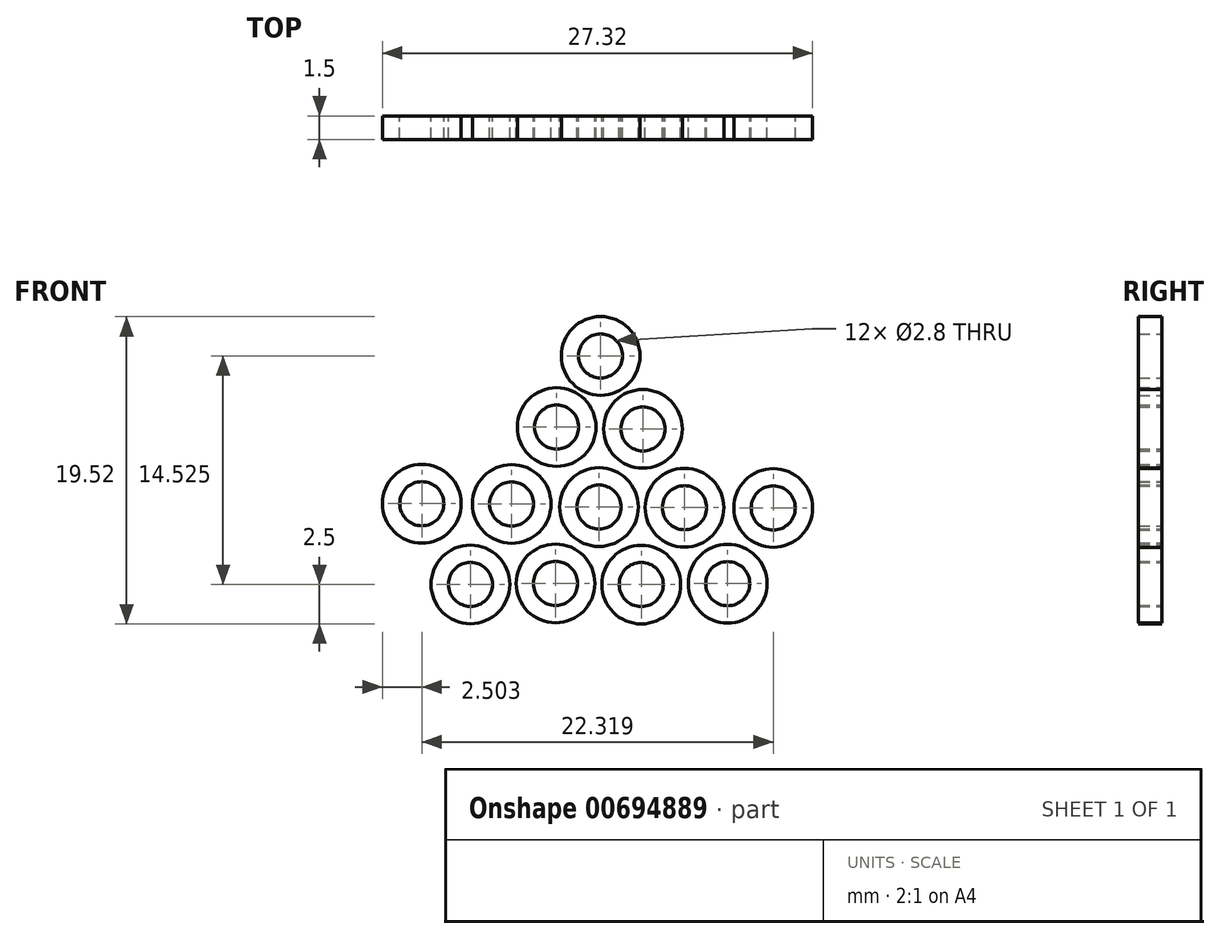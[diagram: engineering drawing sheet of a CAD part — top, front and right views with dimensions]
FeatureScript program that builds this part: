
annotation { "Feature Type Name" : "Feature", "Feature Type Description" : "" }
export const myFeature = defineFeature(function(context is Context, id is Id, definition is map)
    precondition{}
    {
        {
            var Q0;
            Q0=qCreatedBy(makeId("Front.planeOp"),FACE);
            var sketch = newSketch(context, id + "F0", { "sketchPlane" : qUnion([Q0])});
            skCircle(sketch, "E0", {"center": v(0, 0) * mm, "radius": 2.5 * mm});
            skCircle(sketch, "E1", {"center": v(0, 0) * mm, "radius": 1.4 * mm});
            skCircle(sketch, "E2", {"center": v(-2.68, 4.92) * mm, "radius": 2.5 * mm});
            skCircle(sketch, "E3", {"center": v(-2.68, 4.92) * mm, "radius": 1.4 * mm});
            skCircle(sketch, "E4", {"center": v(-5.44, 0.07) * mm, "radius": 2.5 * mm});
            skCircle(sketch, "E5", {"center": v(-5.44, 0.07) * mm, "radius": 1.4 * mm});
            skCircle(sketch, "E6", {"center": v(-13.94, 5.14) * mm, "radius": 2.5 * mm});
            skCircle(sketch, "E7", {"center": v(-13.94, 5.14) * mm, "radius": 1.4 * mm});
            skCircle(sketch, "E8", {"center": v(5.5, 0.06) * mm, "radius": 2.5 * mm});
            skCircle(sketch, "E9", {"center": v(5.5, 0.06) * mm, "radius": 1.4 * mm});
            skCircle(sketch, "E10", {"center": v(8.38, 4.87) * mm, "radius": 2.5 * mm});
            skCircle(sketch, "E11", {"center": v(8.38, 4.87) * mm, "radius": 1.4 * mm});
            skCircle(sketch, "E12", {"center": v(-5.37, 10) * mm, "radius": 2.5 * mm});
            skCircle(sketch, "E13", {"center": v(-5.37, 10) * mm, "radius": 1.4 * mm});
            skCircle(sketch, "E14", {"center": v(0.1, 9.9) * mm, "radius": 2.5 * mm});
            skCircle(sketch, "E15", {"center": v(0.1, 9.9) * mm, "radius": 1.4 * mm});
            skCircle(sketch, "E16", {"center": v(2.75, 4.88) * mm, "radius": 2.5 * mm});
            skCircle(sketch, "E17", {"center": v(2.75, 4.88) * mm, "radius": 1.4 * mm});
            skCircle(sketch, "E18", {"center": v(-8.23, 5.12) * mm, "radius": 2.5 * mm});
            skCircle(sketch, "E19", {"center": v(-8.23, 5.12) * mm, "radius": 1.4 * mm});
            skCircle(sketch, "E20", {"center": v(-10.85, 0.01) * mm, "radius": 2.5 * mm});
            skCircle(sketch, "E21", {"center": v(-10.85, 0.01) * mm, "radius": 1.4 * mm});
            skCircle(sketch, "E22", {"center": v(-2.58, 14.52) * mm, "radius": 2.5 * mm});
            skCircle(sketch, "E23", {"center": v(-2.58, 14.52) * mm, "radius": 1.4 * mm});
            skSolve(sketch);
        }
        {
            var Q0;
            Q0=makeQuery(id+"F0.imprint","IMPRINT",FACE,{"disambiguationData":[TD([[makeQuery(id+"F0.imprint","IMPRINT",EDGE,{"derivedFrom":sQuery(id+"F0.wireOp",EDGE,"E6")}),1.0]])]});
            var Q1;
            Q1=makeQuery(id+"F0.imprint","IMPRINT",FACE,{"disambiguationData":[TD([[makeQuery(id+"F0.imprint","IMPRINT",EDGE,{"derivedFrom":sQuery(id+"F0.wireOp",EDGE,"E18")}),1.0]])]});
            var Q2;
            Q2=makeQuery(id+"F0.imprint","IMPRINT",FACE,{"disambiguationData":[TD([[makeQuery(id+"F0.imprint","IMPRINT",EDGE,{"derivedFrom":sQuery(id+"F0.wireOp",EDGE,"E12")}),1.0]])]});
            var Q3;
            Q3=makeQuery(id+"F0.imprint","IMPRINT",FACE,{"disambiguationData":[TD([[makeQuery(id+"F0.imprint","IMPRINT",EDGE,{"derivedFrom":sQuery(id+"F0.wireOp",EDGE,"E22")}),1.0]])]});
            var Q4;
            Q4=makeQuery(id+"F0.imprint","IMPRINT",FACE,{"disambiguationData":[TD([[makeQuery(id+"F0.imprint","IMPRINT",EDGE,{"derivedFrom":sQuery(id+"F0.wireOp",EDGE,"E14")}),1.0]])]});
            var Q5;
            Q5=makeQuery(id+"F0.imprint","IMPRINT",FACE,{"disambiguationData":[TD([[makeQuery(id+"F0.imprint","IMPRINT",EDGE,{"derivedFrom":sQuery(id+"F0.wireOp",EDGE,"E2")}),1.0]])]});
            var Q6;
            Q6=makeQuery(id+"F0.imprint","IMPRINT",FACE,{"disambiguationData":[TD([[makeQuery(id+"F0.imprint","IMPRINT",EDGE,{"derivedFrom":sQuery(id+"F0.wireOp",EDGE,"E20")}),1.0]])]});
            var Q7;
            Q7=makeQuery(id+"F0.imprint","IMPRINT",FACE,{"disambiguationData":[TD([[makeQuery(id+"F0.imprint","IMPRINT",EDGE,{"derivedFrom":sQuery(id+"F0.wireOp",EDGE,"E4")}),1.0]])]});
            var Q8;
            Q8=makeQuery(id+"F0.imprint","IMPRINT",FACE,{"disambiguationData":[TD([[makeQuery(id+"F0.imprint","IMPRINT",EDGE,{"derivedFrom":sQuery(id+"F0.wireOp",EDGE,"E0")}),1.0]])]});
            var Q9;
            Q9=makeQuery(id+"F0.imprint","IMPRINT",FACE,{"disambiguationData":[TD([[makeQuery(id+"F0.imprint","IMPRINT",EDGE,{"derivedFrom":sQuery(id+"F0.wireOp",EDGE,"E16")}),1.0]])]});
            var Q10;
            Q10=makeQuery(id+"F0.imprint","IMPRINT",FACE,{"disambiguationData":[TD([[makeQuery(id+"F0.imprint","IMPRINT",EDGE,{"derivedFrom":sQuery(id+"F0.wireOp",EDGE,"E10")}),1.0]])]});
            var Q11;
            Q11=makeQuery(id+"F0.imprint","IMPRINT",FACE,{"disambiguationData":[TD([[makeQuery(id+"F0.imprint","IMPRINT",EDGE,{"derivedFrom":sQuery(id+"F0.wireOp",EDGE,"E8")}),1.0]])]});
            extrude(context, id + "F1", {"entities" : qUnion([Q0, Q1, Q2, Q3, Q4, Q5, Q6, Q7, Q8, Q9, Q10, Q11]), "depth" : 1.5 * mm, "offsetDistance" : 25 * mm});
        }
    });
